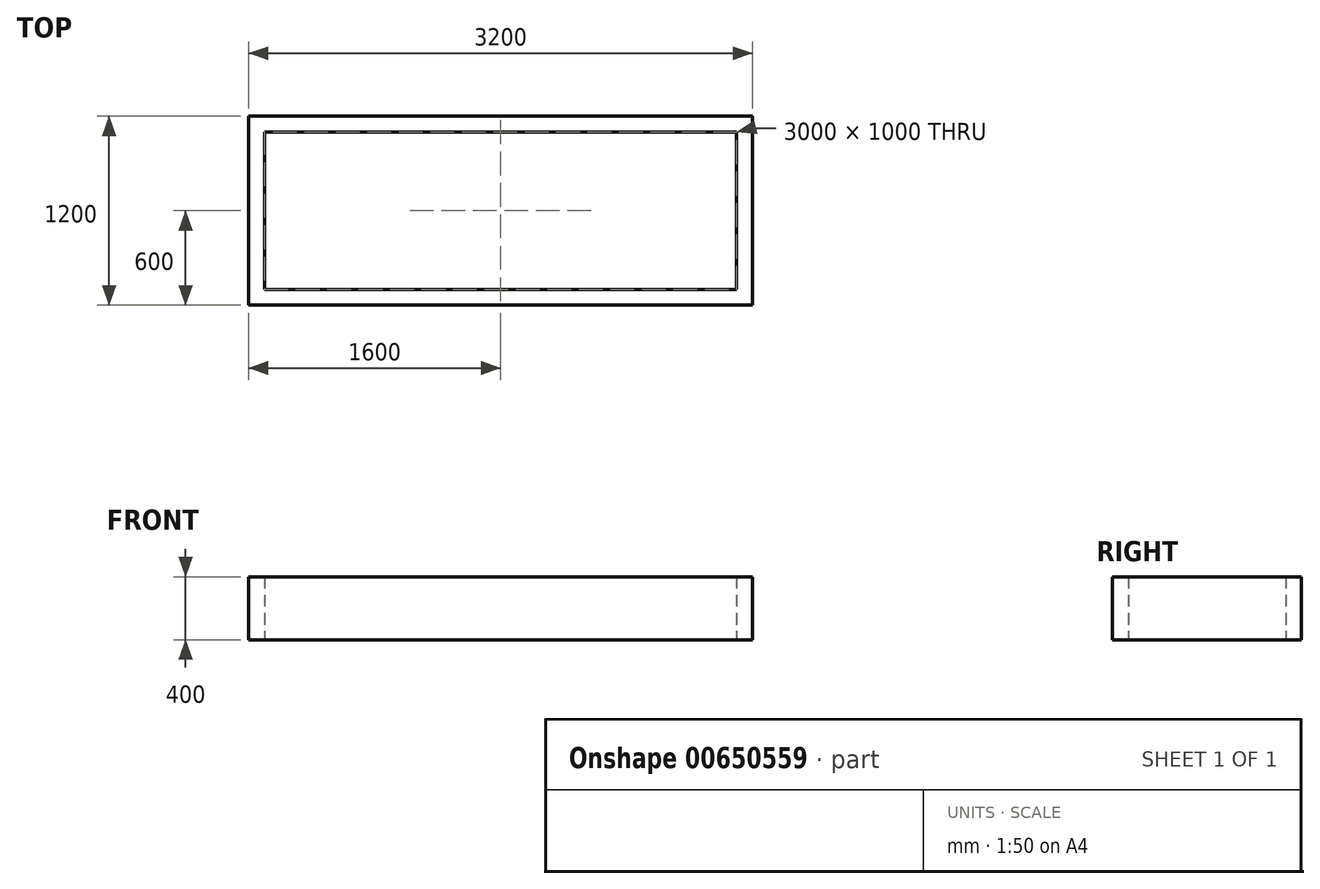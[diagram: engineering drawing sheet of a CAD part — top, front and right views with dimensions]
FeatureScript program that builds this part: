
annotation { "Feature Type Name" : "Feature", "Feature Type Description" : "" }
export const myFeature = defineFeature(function(context is Context, id is Id, definition is map)
    precondition{}
    {
        {
            var Q0;
            Q0=qCreatedBy(makeId("Top.planeOp"),FACE);
            var sketch = newSketch(context, id + "F0", { "sketchPlane" : qUnion([Q0]), "disableImprinting" : false});
            skLineSegment(sketch, "E0.bottom", {"start": v(0, 0) * mm, "end": v(-3200, 0) * mm});
            skLineSegment(sketch, "E0.top", {"start": v(0, 1200) * mm, "end": v(-3200, 1200) * mm});
            skLineSegment(sketch, "E0.left", {"start": v(0, 0) * mm, "end": v(0, 1200) * mm});
            skLineSegment(sketch, "E0.right", {"start": v(-3200, 0) * mm, "end": v(-3200, 1200) * mm});
            skLineSegment(sketch, "E1.bottom", {"start": v(-100, 100) * mm, "end": v(-3100, 100) * mm});
            skLineSegment(sketch, "E1.top", {"start": v(-100, 1100) * mm, "end": v(-3100, 1100) * mm});
            skLineSegment(sketch, "E1.left", {"start": v(-100, 100) * mm, "end": v(-100, 1100) * mm});
            skLineSegment(sketch, "E1.right", {"start": v(-3100, 100) * mm, "end": v(-3100, 1100) * mm});
            skSolve(sketch);
        }
        {
            var Q0;
            Q0 = qSketchRegion(id + "F0", true);
            extrude(context, id + "F1", {"entities" : qUnion([Q0]), "depth" : 400 * mm, "offsetDistance" : 25 * mm});
        }
    });
